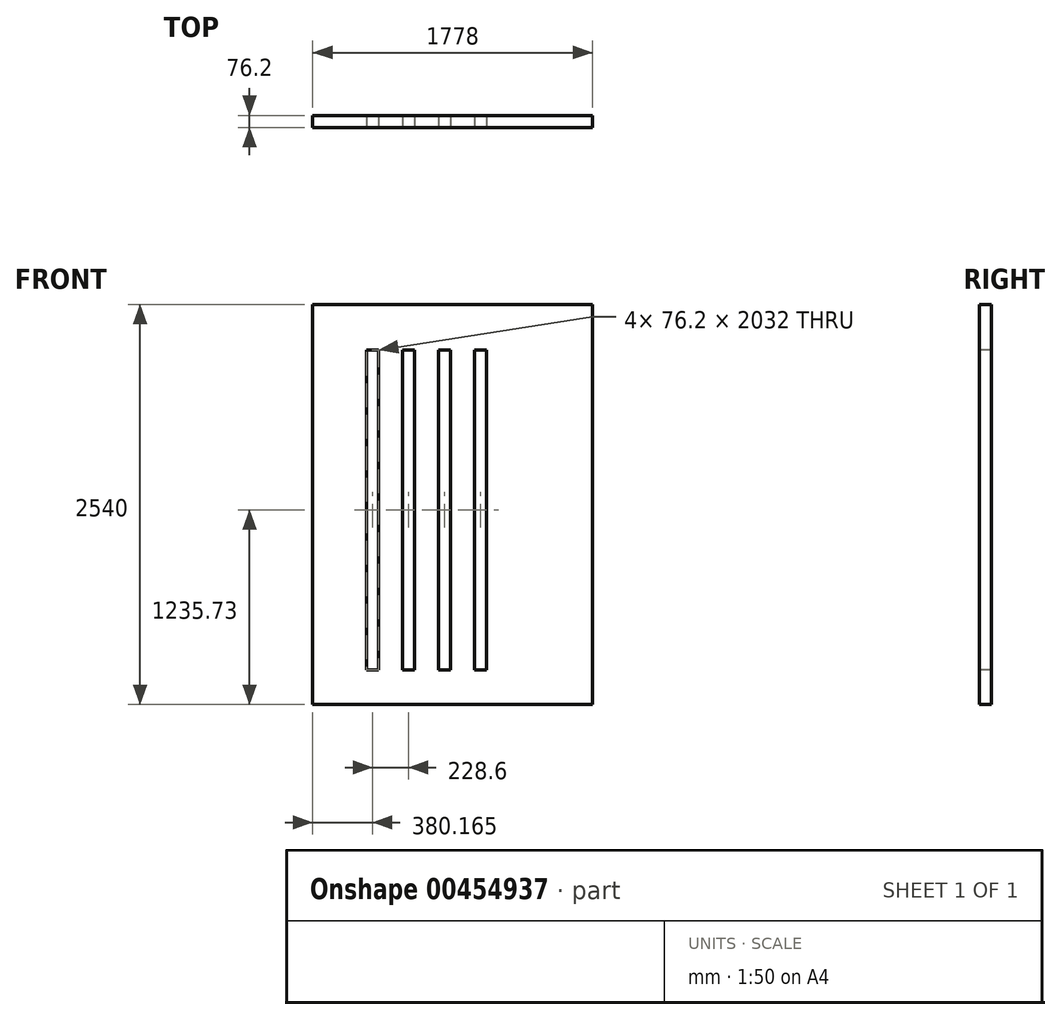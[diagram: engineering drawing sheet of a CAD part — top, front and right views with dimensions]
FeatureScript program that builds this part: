
annotation { "Feature Type Name" : "Feature", "Feature Type Description" : "" }
export const myFeature = defineFeature(function(context is Context, id is Id, definition is map)
    precondition{}
    {
        {
            var Q0;
            Q0=qCreatedBy(makeId("Front.planeOp"),FACE);
            var sketch = newSketch(context, id + "F0", { "sketchPlane" : qUnion([Q0])});
            skLineSegment(sketch, "E0.bottom", {"start": v(-889.14, 1681.59) * mm, "end": v(888.86, 1681.59) * mm});
            skLineSegment(sketch, "E0.top", {"start": v(-889.14, -858.41) * mm, "end": v(888.86, -858.41) * mm});
            skLineSegment(sketch, "E0.left", {"start": v(-889.14, 1681.59) * mm, "end": v(-889.14, -858.41) * mm});
            skLineSegment(sketch, "E0.right", {"start": v(888.86, 1681.59) * mm, "end": v(888.86, -858.41) * mm});
            skSolve(sketch);
        }
        {
            var Q0;
            Q0=makeQuery(id+"F0.imprint","IMPRINT",FACE,{"disambiguationData":[TD([[makeQuery(id+"F0.imprint","IMPRINT",EDGE,{"derivedFrom":sQuery(id+"F0.wireOp",EDGE,"E0.bottom")}),-1.0]])]});
            extrude(context, id + "F1", {"entities" : qUnion([Q0]), "depth" : 76.2 * mm});
        }
        {
            var Q0;
            Q0=makeQuery(id+"F1.opExtrude","CAP_FACE",FACE,{"disambiguationData":[OSD([sQuery(id+"F0.wireOp",EDGE,"E0.bottom"),sQuery(id+"F0.wireOp",EDGE,"E0.top"),sQuery(id+"F0.wireOp",EDGE,"E0.left"),sQuery(id+"F0.wireOp",EDGE,"E0.right")])],"isStart":false});
            var sketch = newSketch(context, id + "F2", { "sketchPlane" : qUnion([Q0])});
            skLineSegment(sketch, "E1.bottom", {"start": v(-547.08, 1393.32) * mm, "end": v(-470.88, 1393.32) * mm});
            skLineSegment(sketch, "E1.top", {"start": v(-547.08, -638.68) * mm, "end": v(-470.88, -638.68) * mm});
            skLineSegment(sketch, "E1.left", {"start": v(-547.08, 1393.32) * mm, "end": v(-547.08, -638.68) * mm});
            skLineSegment(sketch, "E1.right", {"start": v(-470.88, 1393.32) * mm, "end": v(-470.88, -638.68) * mm});
            skLineSegment(sketch, "E2.bottom", {"start": v(-318.48, 1393.32) * mm, "end": v(-242.28, 1393.32) * mm});
            skLineSegment(sketch, "E2.top", {"start": v(-318.48, -638.68) * mm, "end": v(-242.28, -638.68) * mm});
            skLineSegment(sketch, "E2.left", {"start": v(-318.48, 1393.32) * mm, "end": v(-318.48, -638.68) * mm});
            skLineSegment(sketch, "E2.right", {"start": v(-242.28, 1393.32) * mm, "end": v(-242.28, -638.68) * mm});
            skLineSegment(sketch, "E3.bottom", {"start": v(-89.88, 1393.32) * mm, "end": v(-13.68, 1393.32) * mm});
            skLineSegment(sketch, "E3.top", {"start": v(-89.88, -638.68) * mm, "end": v(-13.68, -638.68) * mm});
            skLineSegment(sketch, "E3.left", {"start": v(-89.88, 1393.32) * mm, "end": v(-89.88, -638.68) * mm});
            skLineSegment(sketch, "E3.right", {"start": v(-13.68, 1393.32) * mm, "end": v(-13.68, -638.68) * mm});
            skLineSegment(sketch, "E4.bottom", {"start": v(138.72, 1393.32) * mm, "end": v(214.92, 1393.32) * mm});
            skLineSegment(sketch, "E4.top", {"start": v(138.72, -638.68) * mm, "end": v(214.92, -638.68) * mm});
            skLineSegment(sketch, "E4.left", {"start": v(138.72, 1393.32) * mm, "end": v(138.72, -638.68) * mm});
            skLineSegment(sketch, "E4.right", {"start": v(214.92, 1393.32) * mm, "end": v(214.92, -638.68) * mm});
            skSolve(sketch);
        }
        {
            var Q0;
            Q0=makeQuery(id+"F2.imprint","IMPRINT",FACE,{"disambiguationData":[TD([[makeQuery(id+"F2.imprint","IMPRINT",EDGE,{"derivedFrom":sQuery(id+"F2.wireOp",EDGE,"E1.bottom")}),-1.0]])]});
            var Q1;
            Q1=makeQuery(id+"F2.imprint","IMPRINT",FACE,{"disambiguationData":[TD([[makeQuery(id+"F2.imprint","IMPRINT",EDGE,{"derivedFrom":sQuery(id+"F2.wireOp",EDGE,"E2.bottom")}),-1.0]])]});
            var Q2;
            Q2=makeQuery(id+"F2.imprint","IMPRINT",FACE,{"disambiguationData":[TD([[makeQuery(id+"F2.imprint","IMPRINT",EDGE,{"derivedFrom":sQuery(id+"F2.wireOp",EDGE,"E3.bottom")}),-1.0]])]});
            var Q3;
            Q3=makeQuery(id+"F2.imprint","IMPRINT",FACE,{"disambiguationData":[TD([[makeQuery(id+"F2.imprint","IMPRINT",EDGE,{"derivedFrom":sQuery(id+"F2.wireOp",EDGE,"E4.bottom")}),-1.0]])]});
            extrude(context, id + "F3", {"entities" : qUnion([Q0, Q1, Q2, Q3]), "operationType" : NewBodyOperationType.REMOVE, "endBound" : BoundingType.THROUGH_ALL, "oppositeDirection" : true, "depth" : 25.4 * mm});
        }
    });
